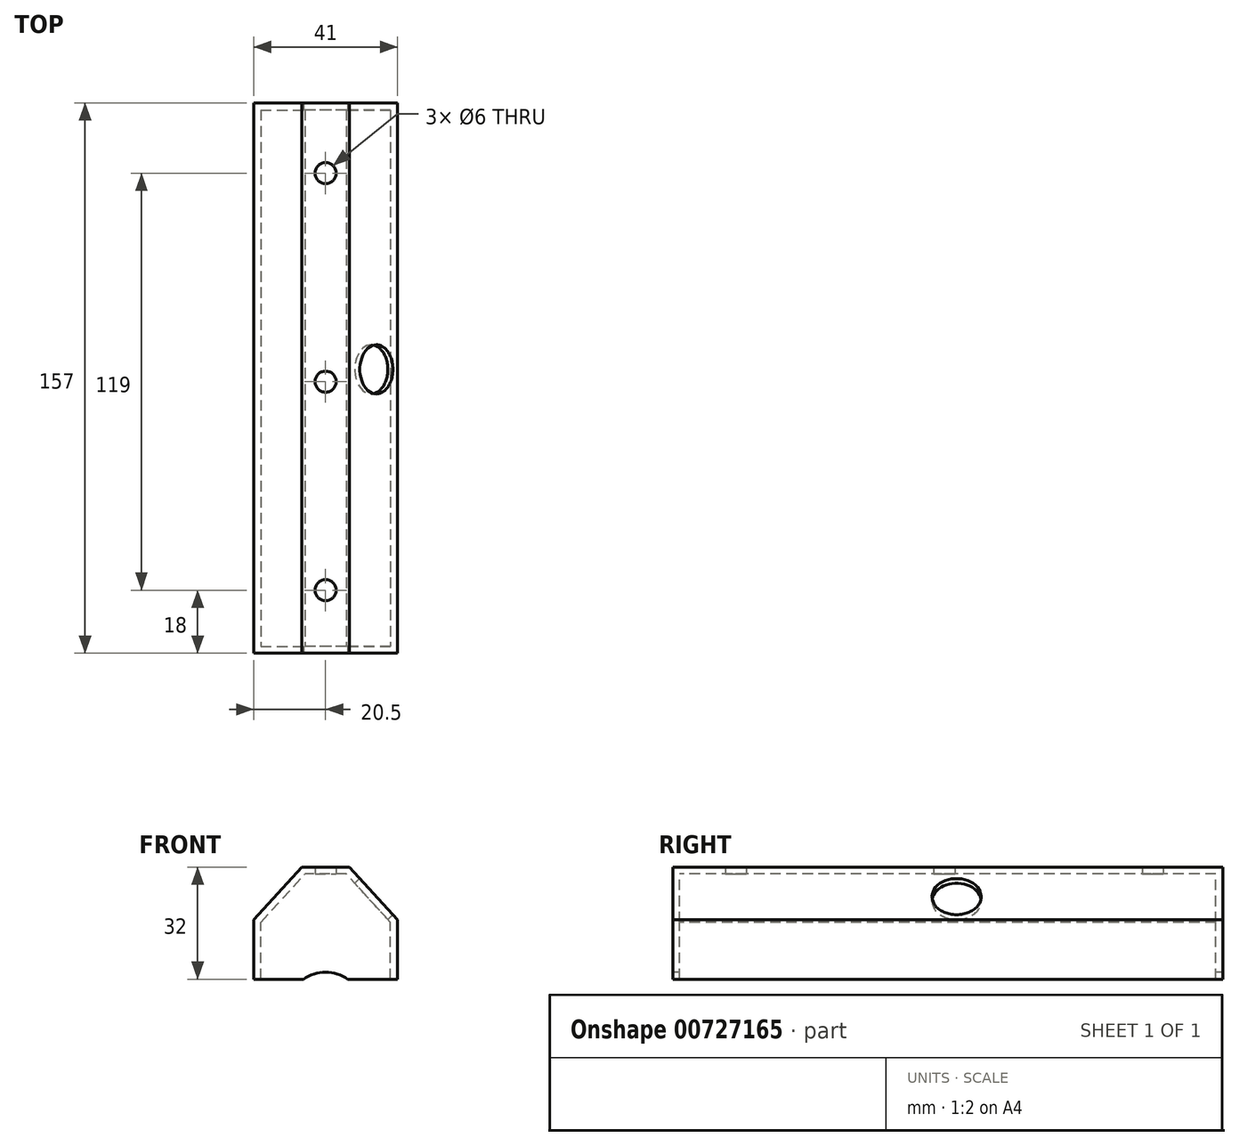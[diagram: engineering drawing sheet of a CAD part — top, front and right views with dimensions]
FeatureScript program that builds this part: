
annotation { "Feature Type Name" : "Feature", "Feature Type Description" : "" }
export const myFeature = defineFeature(function(context is Context, id is Id, definition is map)
    precondition{}
    {
        {
            var Q0;
            Q0=qCreatedBy(makeId("Front.planeOp"),FACE);
            var sketch = newSketch(context, id + "F0", { "sketchPlane" : qUnion([Q0])});
            skLineSegment(sketch, "E0.bottom", {"start": v(-20.5, 0) * mm, "end": v(0, 0) * mm});
            skLineSegment(sketch, "E0.left", {"start": v(-20.5, 0) * mm, "end": v(-20.5, 17) * mm});
            skLineSegment(sketch, "E1.bottom", {"start": v(-6.75, 32) * mm, "end": v(0, 32) * mm});
            skLineSegment(sketch, "E2", {"start": v(-20.5, 17) * mm, "end": v(-6.75, 32) * mm});
            skLineSegment(sketch, "E3.MirrorCS", {"start": v(20.5, 17) * mm, "end": v(6.75, 32) * mm});
            skLineSegment(sketch, "E4.MirrorCS", {"start": v(20.5, 0) * mm, "end": v(20.5, 17) * mm});
            skLineSegment(sketch, "E5.MirrorCS", {"start": v(6.75, 32) * mm, "end": v(0, 32) * mm});
            skLineSegment(sketch, "E6.MirrorCS", {"start": v(20.5, 0) * mm, "end": v(0, 0) * mm});
            skSolve(sketch);
        }
        {
            var Q0;
            Q0=makeQuery(id+"F0.imprint","IMPRINT",FACE,{"disambiguationData":[TD([[makeQuery(id+"F0.imprint","IMPRINT",EDGE,{"derivedFrom":sQuery(id+"F0.wireOp",EDGE,"E0.bottom")}),1.0]])]});
            var Q1;
            Q1=sQuery(id+"F0.wireOp",EDGE,"E4.MirrorCS");
            var Q2;
            Q2=sQuery(id+"F0.wireOp",EDGE,"E3.MirrorCS");
            var Q3;
            Q3=sQuery(id+"F0.wireOp",EDGE,"E5.MirrorCS");
            var Q4;
            Q4=sQuery(id+"F0.wireOp",EDGE,"E1.bottom");
            var Q5;
            Q5=sQuery(id+"F0.wireOp",EDGE,"E2");
            var Q6;
            Q6=sQuery(id+"F0.wireOp",EDGE,"E0.left");
            extrude(context, id + "F1", {"entities" : qUnion([Q0]), "surfaceEntities" : qUnion([Q1, Q2, Q3, Q4, Q5, Q6]), "oppositeDirection" : true, "depth" : 157 * mm, "offsetDistance" : 25 * mm});
        }
        {
            var Q0;
            Q0=makeQuery(id+"F1.opExtrude","SWEPT_FACE",FACE,{"disambiguationData":[OSD([sQuery(id+"F0.wireOp",EDGE,"E0.bottom"),sQuery(id+"F0.wireOp",EDGE,"E6.MirrorCS")])]});
            shell(context, id + "F2", {"entities" : qUnion([Q0]), "thickness" : 2 * mm});
        }
        {
            var Q0;
            Q0=qCreatedBy(makeId("Front.planeOp"),FACE);
            var sketch = newSketch(context, id + "F3", { "sketchPlane" : qUnion([Q0])});
            skCircle(sketch, "E7", {"center": v(0, -9) * mm, "radius": 11 * mm});
            skSolve(sketch);
        }
        {
            var Q0;
            Q0=makeQuery(id+"F3.imprint","IMPRINT",FACE,{"disambiguationData":[TD([[makeQuery(id+"F3.imprint","IMPRINT",EDGE,{"derivedFrom":sQuery(id+"F3.wireOp",EDGE,"E7")}),1.0]])]});
            extrude(context, id + "F4", {"entities" : qUnion([Q0]), "operationType" : NewBodyOperationType.REMOVE, "oppositeDirection" : true, "depth" : 157 * mm, "offsetDistance" : 25 * mm});
        }
        {
            var Q0;
            Q0=makeQuery(id+"F2.opShell","OFFSET_FACE",FACE,{"disambiguationData":[OSD([sQuery(id+"F0.wireOp",EDGE,"E1.bottom"),sQuery(id+"F0.wireOp",EDGE,"E5.MirrorCS")])]});
            var sketch = newSketch(context, id + "F5", { "sketchPlane" : qUnion([Q0])});
            skPoint(sketch, "E8", {"position": v(0, -137) * mm});
            skPoint(sketch, "E9.0.1.0", {"position": v(0, -77.5) * mm});
            skPoint(sketch, "E9.0.2.0", {"position": v(0, -18) * mm});
            skLineSegment(sketch, "E9.direction1", {"start": v(0, -137) * mm, "end": v(59.5, -137) * mm, "construction": true});
            skLineSegment(sketch, "E9.direction2", {"start": v(0, -137) * mm, "end": v(0, -77.5) * mm, "construction": true});
            skSolve(sketch);
        }
        {
            var Q0;
            Q0=sQuery(id+"F5.wireOp",VERTEX,"E9.0.2.0");
            var Q1;
            Q1=sQuery(id+"F5.wireOp",VERTEX,"E9.0.1.0");
            var Q2;
            Q2=sQuery(id+"F5.wireOp",VERTEX,"E8");
            var Q3;
            Q3=makeQuery(id+"F1.opExtrude","SWEPT_BODY",BODY,{"disambiguationData":[OSD([sQuery(id+"F0.wireOp",EDGE,"E0.bottom"),sQuery(id+"F0.wireOp",EDGE,"E0.left"),sQuery(id+"F0.wireOp",EDGE,"E1.bottom"),sQuery(id+"F0.wireOp",EDGE,"E2"),sQuery(id+"F0.wireOp",EDGE,"E3.MirrorCS"),sQuery(id+"F0.wireOp",EDGE,"E4.MirrorCS"),sQuery(id+"F0.wireOp",EDGE,"E5.MirrorCS"),sQuery(id+"F0.wireOp",EDGE,"E6.MirrorCS")])]});
            hole(context, id + "F6", {"style" : HoleStyle.SIMPLE, "endStyle" : HoleEndStyle.THROUGH, "holeDiameter" : 6 * mm, "majorDiameter" : 5 * mm, "isTappedThrough" : true, "tappedDepth" : 12 * mm, "tapClearance" : 3, "locations" : qUnion([Q0, Q1, Q2]), "scope" : qUnion([Q3])});
        }
        {
            var Q0;
            Q0=makeQuery(id+"F1.opExtrude","SWEPT_FACE",FACE,{"disambiguationData":[OSD([sQuery(id+"F0.wireOp",EDGE,"E3.MirrorCS")])]});
            var sketch = newSketch(context, id + "F7", { "sketchPlane" : qUnion([Q0])});
            skPoint(sketch, "E10", {"position": v(81.01, 7.57) * mm});
            skCircle(sketch, "E11", {"center": v(81.01, 7.57) * mm, "radius": 7 * mm});
            skSolve(sketch);
        }
        {
            var Q0;
            Q0 = qSketchRegion(id + "F7", true);
            extrude(context, id + "F8", {"entities" : qUnion([Q0]), "operationType" : NewBodyOperationType.REMOVE, "oppositeDirection" : true, "depth" : 3 * mm, "offsetDistance" : 25 * mm});
        }
    });
